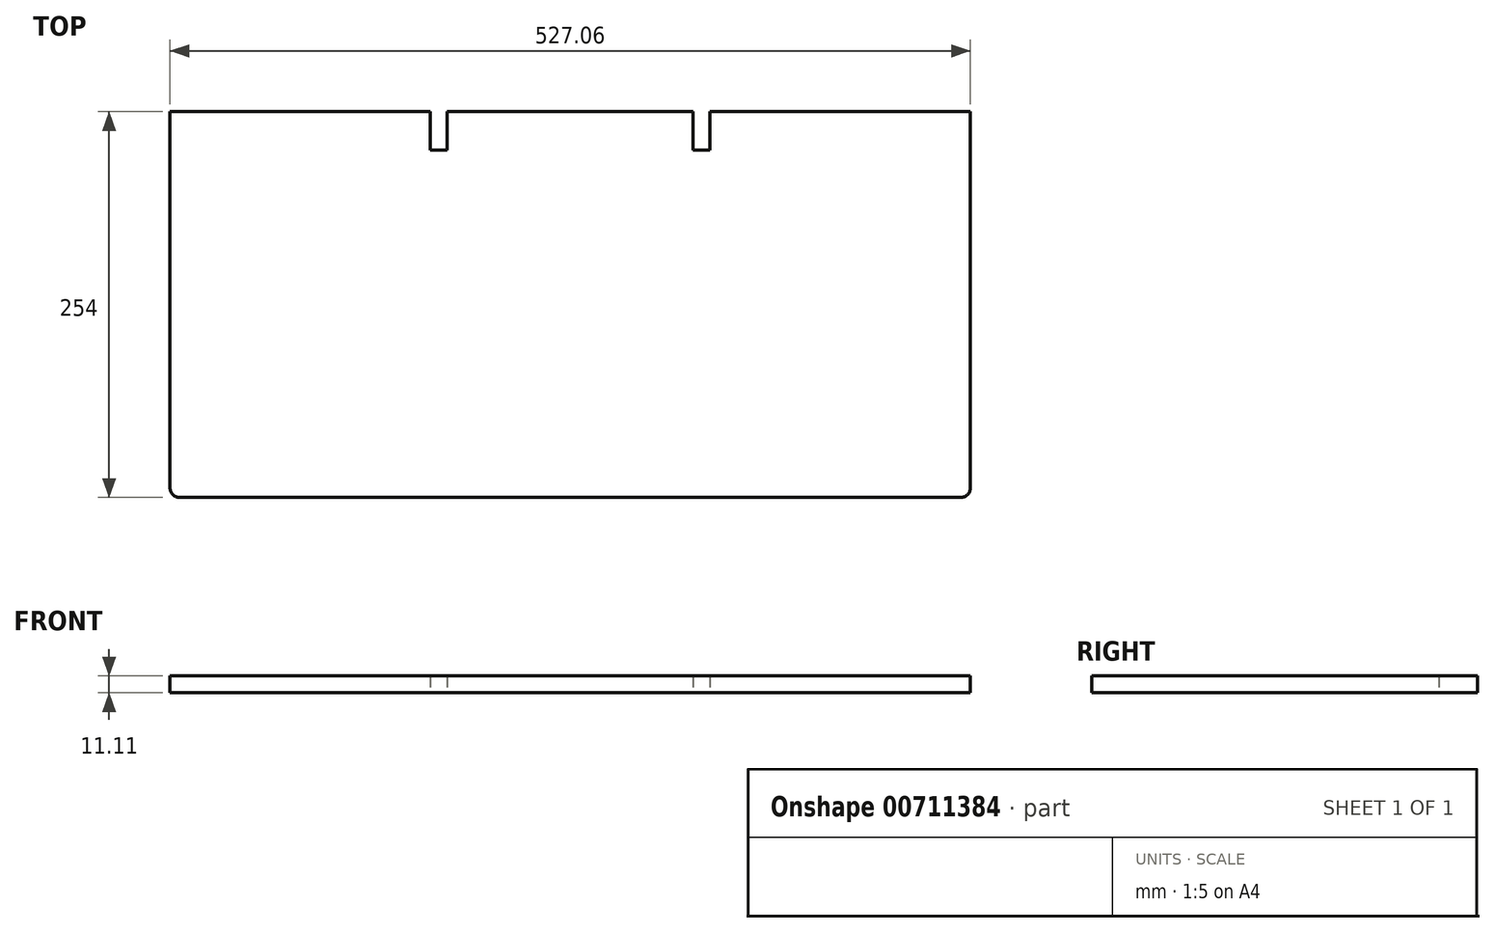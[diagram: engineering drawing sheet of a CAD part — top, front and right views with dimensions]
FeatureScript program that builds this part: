
annotation { "Feature Type Name" : "Feature", "Feature Type Description" : "" }
export const myFeature = defineFeature(function(context is Context, id is Id, definition is map)
    precondition{}
    {
        {
            var Q0;
            Q0=qCreatedBy(makeId("Top.planeOp"),FACE);
            var sketch = newSketch(context, id + "F0", { "sketchPlane" : qUnion([Q0])});
            skLineSegment(sketch, "E0.bottom", {"start": v(-263.53, -127) * mm, "end": v(263.53, -127) * mm});
            skLineSegment(sketch, "E0.top", {"start": v(-263.53, 127) * mm, "end": v(263.53, 127) * mm});
            skLineSegment(sketch, "E0.left", {"start": v(-263.53, -127) * mm, "end": v(-263.53, 127) * mm});
            skLineSegment(sketch, "E0.right", {"start": v(263.53, -127) * mm, "end": v(263.53, 127) * mm});
            skPoint(sketch, "E0.middle", {"position": v(0, 0) * mm});
            skLineSegment(sketch, "E1.bottom", {"start": v(-263.53, 127) * mm, "end": v(-92.07, 127) * mm});
            skLineSegment(sketch, "E1.left", {"start": v(-263.53, 127) * mm, "end": v(-263.53, -101.6) * mm});
            skLineSegment(sketch, "E2.bottom", {"start": v(263.53, 127) * mm, "end": v(92.07, 127) * mm});
            skLineSegment(sketch, "E2.left", {"start": v(263.53, 127) * mm, "end": v(263.53, -101.6) * mm});
            skLineSegment(sketch, "E3.bottom", {"start": v(-92.07, 127) * mm, "end": v(-80.95, 127) * mm});
            skLineSegment(sketch, "E3.top", {"start": v(-92.07, 101.6) * mm, "end": v(-80.95, 101.6) * mm});
            skLineSegment(sketch, "E3.left", {"start": v(-92.07, 127) * mm, "end": v(-92.07, 101.6) * mm});
            skLineSegment(sketch, "E3.right", {"start": v(-80.95, 127) * mm, "end": v(-80.95, 101.6) * mm});
            skLineSegment(sketch, "E4.bottom", {"start": v(92.07, 127) * mm, "end": v(80.95, 127) * mm});
            skLineSegment(sketch, "E4.top", {"start": v(92.08, 101.6) * mm, "end": v(80.95, 101.6) * mm});
            skLineSegment(sketch, "E4.left", {"start": v(92.07, 127) * mm, "end": v(92.08, 101.6) * mm});
            skLineSegment(sketch, "E4.right", {"start": v(80.95, 127) * mm, "end": v(80.95, 101.6) * mm});
            skLineSegment(sketch, "E5.bottom", {"start": v(80.95, 101.6) * mm, "end": v(92.07, 101.6) * mm});
            skLineSegment(sketch, "E5.top", {"start": v(80.95, -127) * mm, "end": v(92.08, -127) * mm});
            skSolve(sketch);
        }
        {
            var Q0;
            {var subQ0=sQuery(id+"F0.wireOp",EDGE,"E0.left");Q0=makeQuery(id+"F0.imprint","IMPRINT",FACE,{"disambiguationData":[TD([[makeQuery(id+"F0.imprint","IMPRINT",EDGE,{"derivedFrom":subQ0}),-1.0]])]});}
            var Q1;
            Q1=makeQuery(id+"F0.imprint","IMPRINT",FACE,{"disambiguationData":[TD([[makeQuery(id+"F0.imprint","IMPRINT",EDGE,{"derivedFrom":sQuery(id+"F0.wireOp",EDGE,"nsXebuqk-dGNw-oNUx-tXBs-1cNWmNBQbUUd.top")}),1.0]])]});
            var Q2;
            Q2=makeQuery(id+"F0.imprint","IMPRINT",FACE,{"disambiguationData":[TD([[makeQuery(id+"F0.imprint","IMPRINT",EDGE,{"derivedFrom":sQuery(id+"F0.wireOp",EDGE,"E0.top")}),-1.0]])]});
            var Q3;
            Q3=makeQuery(id+"F0.imprint","IMPRINT",FACE,{"disambiguationData":[TD([[makeQuery(id+"F0.imprint","IMPRINT",EDGE,{"derivedFrom":sQuery(id+"F0.wireOp",EDGE,"E5.bottom")}),-1.0]])]});
            var Q4;
            {var subQ0=sQuery(id+"F0.wireOp",EDGE,"E0.right");Q4=makeQuery(id+"F0.imprint","IMPRINT",FACE,{"disambiguationData":[TD([[makeQuery(id+"F0.imprint","IMPRINT",EDGE,{"derivedFrom":subQ0}),1.0]])]});}
            extrude(context, id + "F1", {"entities" : qUnion([Q0, Q1, Q2, Q3, Q4]), "depth" : 11.1 * mm, "offsetDistance" : 25.4 * mm});
        }
        {
            var Q0;
            Q0=makeQuery(id+"F1.opExtrude","SWEPT_EDGE",EDGE,{"disambiguationData":[OSD([sQuery(id+"F0.wireOp",EDGE,"E0.bottom"),sQuery(id+"F0.wireOp",EDGE,"E0.right")])]});
            var Q1;
            Q1=makeQuery(id+"F1.opExtrude","SWEPT_EDGE",EDGE,{"disambiguationData":[OSD([sQuery(id+"F0.wireOp",EDGE,"E2.bottom"),sQuery(id+"F0.wireOp",EDGE,"E2.left")])]});
            var Q2;
            Q2=makeQuery(id+"F1.opExtrude","SWEPT_EDGE",EDGE,{"disambiguationData":[OSD([sQuery(id+"F0.wireOp",EDGE,"E0.bottom"),sQuery(id+"F0.wireOp",EDGE,"E0.left")])]});
            var Q3;
            Q3=makeQuery(id+"F1.opExtrude","SWEPT_EDGE",EDGE,{"disambiguationData":[OSD([sQuery(id+"F0.wireOp",EDGE,"E1.bottom"),sQuery(id+"F0.wireOp",EDGE,"E1.left")])]});
            fillet(context, id + "F2", {"entities" : qUnion([Q0, Q1, Q2, Q3]), "radius" : 6.35 * mm, "tangentPropagation" : true, "allowEdgeOverflow" : false});
        }
    });
